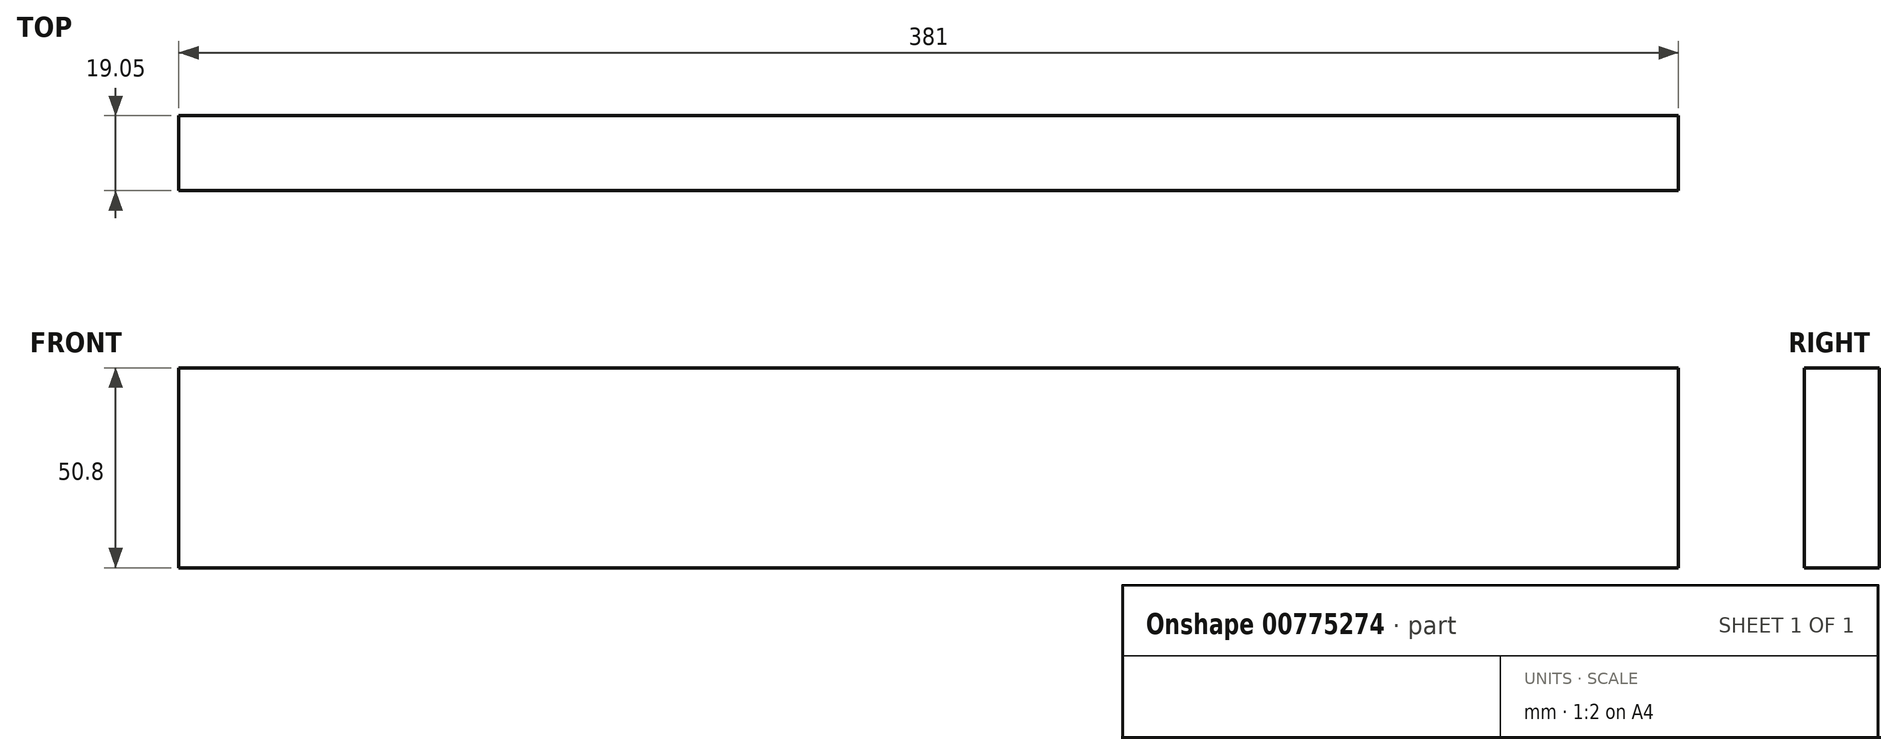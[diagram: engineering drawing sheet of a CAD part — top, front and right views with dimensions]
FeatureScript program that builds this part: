
annotation { "Feature Type Name" : "Feature", "Feature Type Description" : "" }
export const myFeature = defineFeature(function(context is Context, id is Id, definition is map)
    precondition{}
    {
        {
            var Q0;
            Q0=qCreatedBy(makeId("Front.planeOp"),FACE);
            var sketch = newSketch(context, id + "F0", { "sketchPlane" : qUnion([Q0])});
            skLineSegment(sketch, "E0.bottom", {"start": v(0, 0) * mm, "end": v(-381, 0) * mm});
            skLineSegment(sketch, "E0.top", {"start": v(0, 50.8) * mm, "end": v(-381, 50.8) * mm});
            skLineSegment(sketch, "E0.left", {"start": v(0, 0) * mm, "end": v(0, 50.8) * mm});
            skLineSegment(sketch, "E0.right", {"start": v(-381, 0) * mm, "end": v(-381, 50.8) * mm});
            skSolve(sketch);
        }
        {
            var Q0;
            Q0 = qSketchRegion(id + "F0", true);
            extrude(context, id + "F1", {"entities" : qUnion([Q0]), "depth" : 19.05 * mm, "offsetDistance" : 25.4 * mm});
        }
    });
